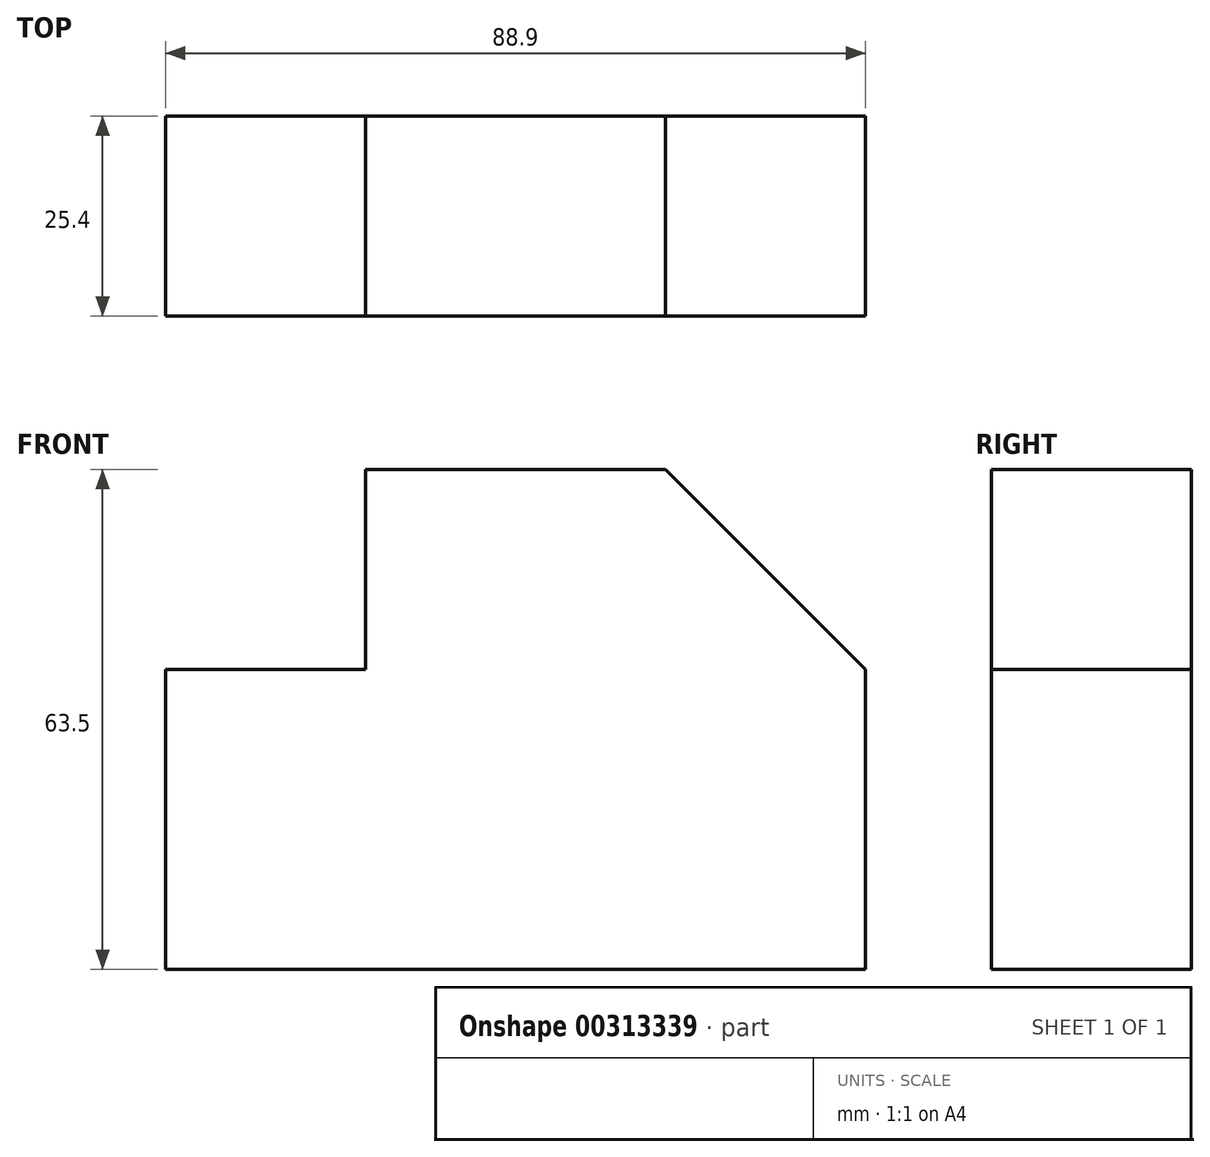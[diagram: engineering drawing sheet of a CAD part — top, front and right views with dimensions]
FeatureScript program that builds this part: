
annotation { "Feature Type Name" : "Feature", "Feature Type Description" : "" }
export const myFeature = defineFeature(function(context is Context, id is Id, definition is map)
    precondition{}
    {
        {
            var Q0;
            Q0=qCreatedBy(makeId("Front.planeOp"),FACE);
            var sketch = newSketch(context, id + "F0", { "sketchPlane" : qUnion([Q0])});
            skLineSegment(sketch, "E0", {"start": v(-38.26, -68.87) * mm, "end": v(50.64, -68.87) * mm});
            skLineSegment(sketch, "E1", {"start": v(-38.26, -68.87) * mm, "end": v(-38.26, -30.77) * mm});
            skLineSegment(sketch, "E2", {"start": v(-38.26, -30.77) * mm, "end": v(-12.86, -30.77) * mm});
            skLineSegment(sketch, "E3", {"start": v(-12.86, -30.77) * mm, "end": v(-12.86, -5.37) * mm});
            skLineSegment(sketch, "E4", {"start": v(-12.86, -5.37) * mm, "end": v(25.24, -5.37) * mm});
            skLineSegment(sketch, "E5", {"start": v(50.64, -68.87) * mm, "end": v(50.64, -30.77) * mm});
            skLineSegment(sketch, "E6", {"start": v(25.24, -5.37) * mm, "end": v(50.64, -30.77) * mm});
            skSolve(sketch);
        }
        {
            var Q0;
            Q0=makeQuery(id+"F0.imprint","IMPRINT",FACE,{"disambiguationData":[TD([[makeQuery(id+"F0.imprint","IMPRINT",EDGE,{"derivedFrom":sQuery(id+"F0.wireOp",EDGE,"E0")}),1.0]])]});
            extrude(context, id + "F1", {"entities" : qUnion([Q0]), "depth" : 25.4 * mm});
        }
    });
